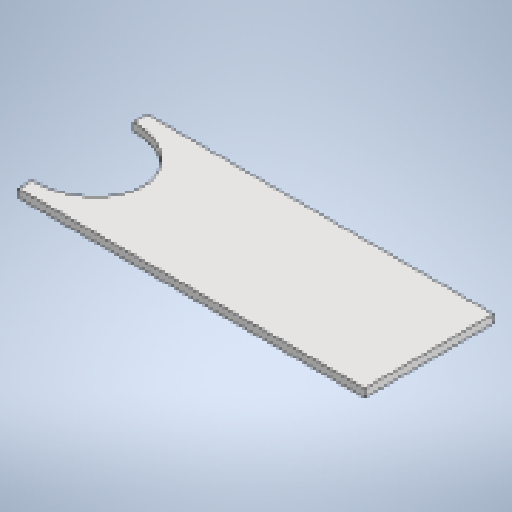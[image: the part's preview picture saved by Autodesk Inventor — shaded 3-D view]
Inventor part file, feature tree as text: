
AUTODESK INVENTOR PART (.ipt)
format: ipt  version: 2025.1 (Build 291241020, 241B)  size: 167,424 bytes
history: native  units: mm
features: other x2, sheet_metal_op x1, sketch x1
ambient origin geometry x8: Origin, YZ Plane, XZ Plane, XY Plane, X Axis, Y Axis, Z Axis, Center Point
bodies: Body1 (feature_tree)
feature tree (4):
  sheet_metal_op  "Face1"
  sketch  "Sketch1"  dims[d12=75.0mm d13=63.0mm d14=160.0mm d15=430.0mm d16=10.0mm]
  other  "Plate1"
  other  "Definition1"
